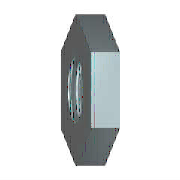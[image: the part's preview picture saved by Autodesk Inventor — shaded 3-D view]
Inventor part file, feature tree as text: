
AUTODESK INVENTOR PART (.ipt)
format: ipt  version: 2017 (Build 210142000, 142)  size: 125,440 bytes
history: native  units: mm (DEFAULTED — no unit token found)
features: other x4, sketch x2, extrude x1, chamfer x1
ambient origin geometry x8: Origin, YZ Plane, XZ Plane, XY Plane, X Axis, Y Axis, Z Axis, Center Point
bodies: Solid1 (feature_tree)
feature tree (8):
  extrude  "Extrusion1"  TaperAngle=0.0deg  [1 undecoded]
  other  "MSC_A1"
  other  "MSC_PT1"
  other  "MSC_PT2"
  other  "MSC_PF1"
  chamfer  "Chamfer1"  [1 undecoded]
  sketch  "Sketch1"  dims[d2=0.0mm]
  sketch  "Sketch2"  dims[d3=2.459mm d4=1.8mm d5=4.0mm d6=2.0mm d7=60.0deg d8=8.0mm d9=20.594885mm d14=0.0mm d15=0.0mm d16=0.0mm d17=0.3mm d18=0.3mm d20=45.0deg d21=0.0mm d23=0.0mm d24=0.0mm d25=0.0mm]
note: 2 required parameter values undecoded (feature->parameter linkage not recoverable at this tier; creation-order binding heuristic only, values carry confidence <= 0.55)
